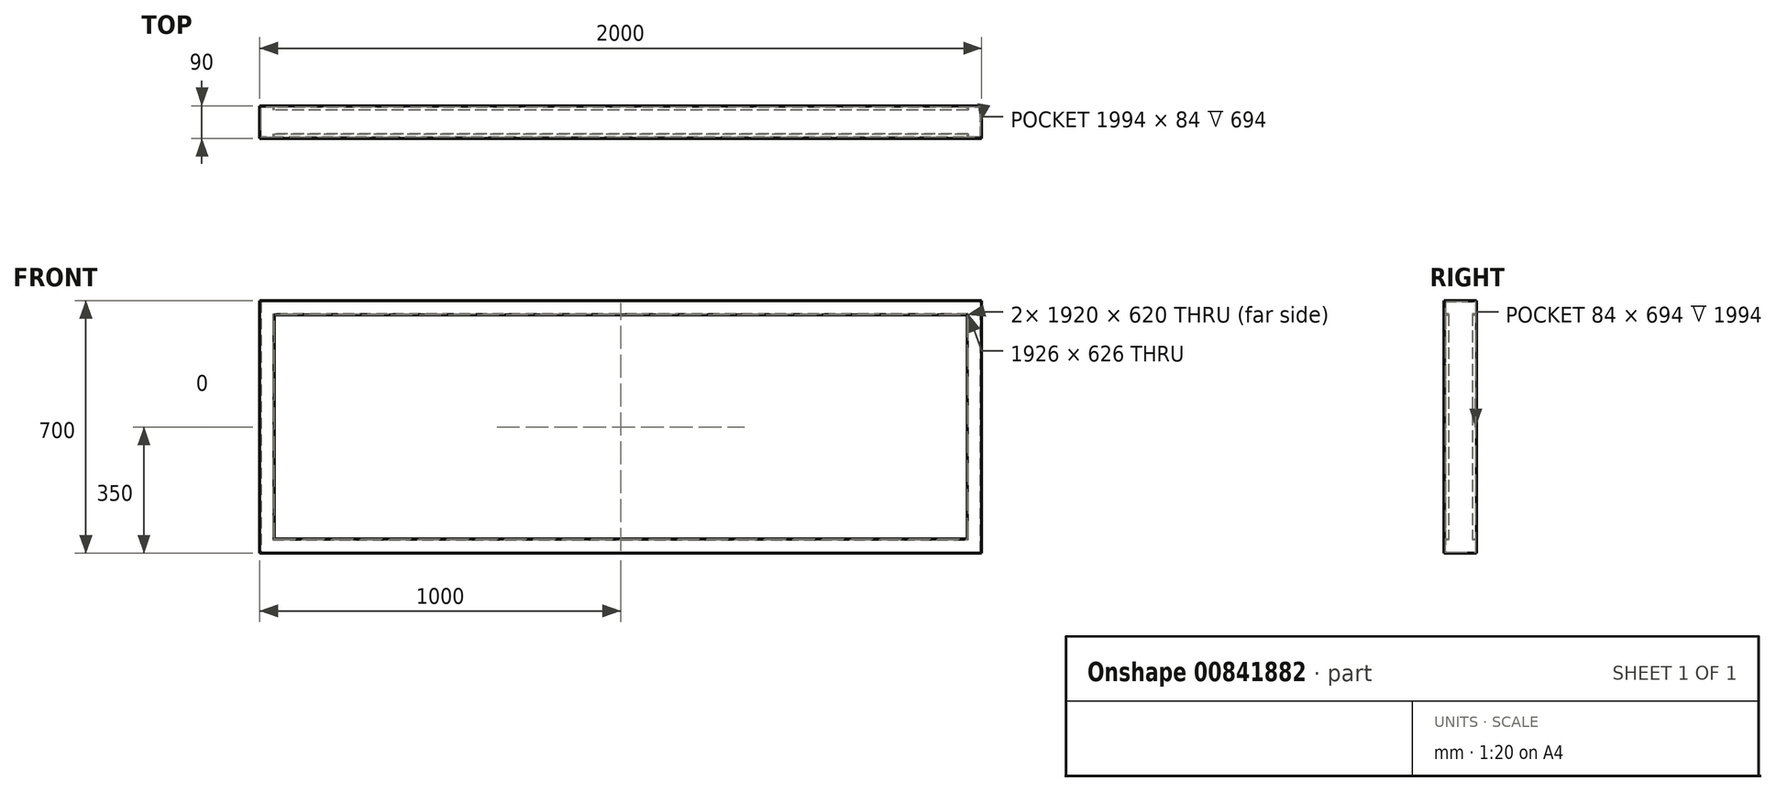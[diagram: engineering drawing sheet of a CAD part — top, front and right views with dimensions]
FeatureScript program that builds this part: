
annotation { "Feature Type Name" : "Feature", "Feature Type Description" : "" }
export const myFeature = defineFeature(function(context is Context, id is Id, definition is map)
    precondition{}
    {
        {
            var Q0;
            Q0=qCreatedBy(makeId("Front.planeOp"),FACE);
            var sketch = newSketch(context, id + "F0", { "sketchPlane" : qUnion([Q0])});
            skLineSegment(sketch, "E0.bottom", {"start": v(0, 0) * mm, "end": v(2000, 0) * mm});
            skLineSegment(sketch, "E0.top", {"start": v(0, 700) * mm, "end": v(2000, 700) * mm});
            skLineSegment(sketch, "E0.left", {"start": v(0, 0) * mm, "end": v(0, 700) * mm});
            skLineSegment(sketch, "E0.right", {"start": v(2000, 0) * mm, "end": v(2000, 700) * mm});
            skSolve(sketch);
        }
        {
            var Q0;
            Q0=qCreatedBy(makeId("Right.planeOp"),FACE);
            var sketch = newSketch(context, id + "F1", { "sketchPlane" : qUnion([Q0])});
            skLineSegment(sketch, "E1", {"start": v(0, 0) * mm, "end": v(-45, 0) * mm});
            skLineSegment(sketch, "E2", {"start": v(-45, 0) * mm, "end": v(-45, 40) * mm});
            skLineSegment(sketch, "E3", {"start": v(-45, 40) * mm, "end": v(-33, 40) * mm});
            skLineSegment(sketch, "E4", {"start": v(0, 0) * mm, "end": v(0, 92.73) * mm, "construction": true});
            skLineSegment(sketch, "E5.MirrorCS", {"start": v(45, 0) * mm, "end": v(45, 40) * mm});
            skLineSegment(sketch, "E6.MirrorCS", {"start": v(0, 0) * mm, "end": v(45, 0) * mm});
            skLineSegment(sketch, "E7.MirrorCS", {"start": v(45, 40) * mm, "end": v(33, 40) * mm});
            skLineSegment(sketch, "E8.0", {"start": v(42, 37) * mm, "end": v(33, 37) * mm});
            skLineSegment(sketch, "E8.1", {"start": v(42, 3) * mm, "end": v(42, 37) * mm});
            skLineSegment(sketch, "E8.2", {"start": v(-42, 37) * mm, "end": v(-33, 37) * mm});
            skLineSegment(sketch, "E8.3", {"start": v(-42, 3) * mm, "end": v(-42, 37) * mm});
            skLineSegment(sketch, "E8.4", {"start": v(0, 3) * mm, "end": v(-42, 3) * mm});
            skLineSegment(sketch, "E8.5", {"start": v(0, 3) * mm, "end": v(42, 3) * mm});
            skLineSegment(sketch, "E9", {"start": v(33, 40) * mm, "end": v(33, 37) * mm});
            skLineSegment(sketch, "E10", {"start": v(-33, 40) * mm, "end": v(-33, 37) * mm});
            skSolve(sketch);
        }
        {
            var Q0;
            Q0 = qSketchRegion(id + "F1", true);
            var Q1;
            Q1=sQuery(id+"F0.wireOp",EDGE,"E0.bottom");
            var Q2;
            Q2=sQuery(id+"F0.wireOp",EDGE,"E0.right");
            var Q3;
            Q3=sQuery(id+"F0.wireOp",EDGE,"E0.top");
            var Q4;
            Q4=sQuery(id+"F0.wireOp",EDGE,"E0.left");
            sweep(context, id + "F2", {"profiles" : qUnion([Q0]), "path" : qUnion([Q1, Q2, Q3, Q4])});
        }
    });
